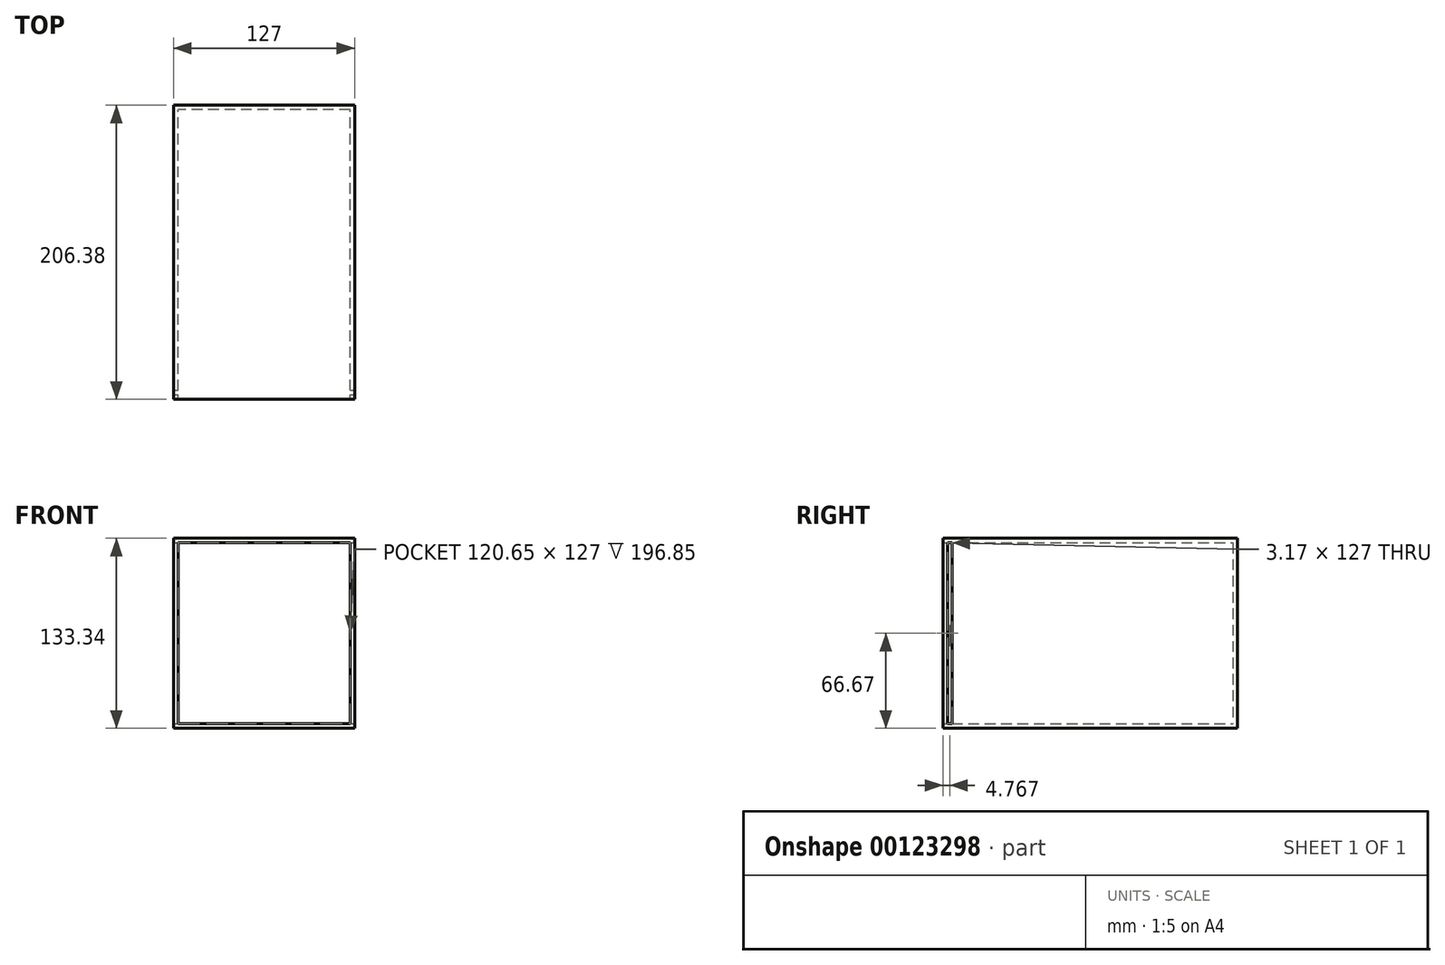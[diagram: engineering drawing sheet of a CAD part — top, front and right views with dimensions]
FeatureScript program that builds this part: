
annotation { "Feature Type Name" : "Feature", "Feature Type Description" : "" }
export const myFeature = defineFeature(function(context is Context, id is Id, definition is map)
    precondition{}
    {
        {
            var Q0;
            Q0=qCreatedBy(makeId("Front.planeOp"),FACE);
            var sketch = newSketch(context, id + "F0", { "sketchPlane" : qUnion([Q0])});
            skLineSegment(sketch, "E0.bottom", {"start": v(63.5, -63.5) * mm, "end": v(-63.5, -63.5) * mm});
            skLineSegment(sketch, "E0.top", {"start": v(63.5, 63.5) * mm, "end": v(-63.5, 63.5) * mm});
            skLineSegment(sketch, "E0.left", {"start": v(63.5, -63.5) * mm, "end": v(63.5, 63.5) * mm});
            skLineSegment(sketch, "E0.right", {"start": v(-63.5, -63.5) * mm, "end": v(-63.5, 63.5) * mm});
            skPoint(sketch, "E0.middle", {"position": v(0, 0) * mm});
            skSolve(sketch);
        }
        {
            var Q0;
            Q0 = qSketchRegion(id + "F0", true);
            extrude(context, id + "F1", {"entities" : qUnion([Q0]), "depth" : 3.17 * mm});
        }
        {
            var Q0;
            Q0=makeQuery(id+"F1.opExtrude","CAP_FACE",FACE,{"disambiguationData":[OSD([sQuery(id+"F0.wireOp",EDGE,"E0.bottom"),sQuery(id+"F0.wireOp",EDGE,"E0.top"),sQuery(id+"F0.wireOp",EDGE,"E0.left"),sQuery(id+"F0.wireOp",EDGE,"E0.right")])],"isStart":false});
            var sketch = newSketch(context, id + "F2", { "sketchPlane" : qUnion([Q0])});
            skLineSegment(sketch, "E1.bottom", {"start": v(-63.5, 63.5) * mm, "end": v(-60.32, 63.5) * mm});
            skLineSegment(sketch, "E1.top", {"start": v(-63.5, -63.5) * mm, "end": v(-60.32, -63.5) * mm});
            skLineSegment(sketch, "E1.left", {"start": v(-63.5, 63.5) * mm, "end": v(-63.5, -63.5) * mm});
            skLineSegment(sketch, "E1.right", {"start": v(-60.32, 63.5) * mm, "end": v(-60.32, -63.5) * mm});
            skLineSegment(sketch, "E2", {"start": v(0, 0) * mm, "end": v(0, 63.5) * mm, "construction": true});
            skLineSegment(sketch, "E3.MirrorCS", {"start": v(60.32, 63.5) * mm, "end": v(60.32, -63.5) * mm});
            skLineSegment(sketch, "E4.MirrorCS", {"start": v(63.5, 63.5) * mm, "end": v(60.32, 63.5) * mm});
            skLineSegment(sketch, "E5.MirrorCS", {"start": v(63.5, 63.5) * mm, "end": v(63.5, -63.5) * mm});
            skLineSegment(sketch, "E6.MirrorCS", {"start": v(63.5, -63.5) * mm, "end": v(60.32, -63.5) * mm});
            skSolve(sketch);
        }
        {
            var Q0;
            Q0 = qSketchRegion(id + "F2", true);
            extrude(context, id + "F3", {"entities" : qUnion([Q0]), "operationType" : NewBodyOperationType.ADD, "depth" : 203.2 * mm});
        }
        {
            var Q0;
            Q0=makeQuery(id+"F3.boolean.opBoolean","MERGE",FACE,{"derivedFrom":[makeQuery(id+"F1.opExtrude","SWEPT_FACE",FACE,{"disambiguationData":[OSD([sQuery(id+"F0.wireOp",EDGE,"E0.top")])]}),makeQuery(id+"F3.opExtrude","SWEPT_FACE",FACE,{"disambiguationData":[OSD([sQuery(id+"F2.wireOp",EDGE,"E1.bottom")])]}),makeQuery(id+"F3.opExtrude","SWEPT_FACE",FACE,{"disambiguationData":[OSD([sQuery(id+"F2.wireOp",EDGE,"E4.MirrorCS")])]})]});
            var sketch = newSketch(context, id + "F4", { "sketchPlane" : qUnion([Q0])});
            skLineSegment(sketch, "E7.bottom", {"start": v(-63.5, 0) * mm, "end": v(63.5, 0) * mm});
            skLineSegment(sketch, "E7.top", {"start": v(-63.5, -206.38) * mm, "end": v(63.5, -206.38) * mm});
            skLineSegment(sketch, "E7.left", {"start": v(-63.5, 0) * mm, "end": v(-63.5, -206.38) * mm});
            skLineSegment(sketch, "E7.right", {"start": v(63.5, 0) * mm, "end": v(63.5, -206.38) * mm});
            skSolve(sketch);
        }
        {
            var Q0;
            Q0 = qSketchRegion(id + "F4", true);
            extrude(context, id + "F5", {"entities" : qUnion([Q0]), "operationType" : NewBodyOperationType.ADD, "depth" : 3.17 * mm});
        }
        {
            var Q0;
            Q0=makeQuery(id+"F3.boolean.opBoolean","MERGE",FACE,{"derivedFrom":[makeQuery(id+"F1.opExtrude","SWEPT_FACE",FACE,{"disambiguationData":[OSD([sQuery(id+"F0.wireOp",EDGE,"E0.bottom")])]}),makeQuery(id+"F3.opExtrude","SWEPT_FACE",FACE,{"disambiguationData":[OSD([sQuery(id+"F2.wireOp",EDGE,"E1.top")])]}),makeQuery(id+"F3.opExtrude","SWEPT_FACE",FACE,{"disambiguationData":[OSD([sQuery(id+"F2.wireOp",EDGE,"E6.MirrorCS")])]})]});
            var sketch = newSketch(context, id + "F6", { "sketchPlane" : qUnion([Q0])});
            skLineSegment(sketch, "E8.bottom", {"start": v(-63.5, 0) * mm, "end": v(63.5, 0) * mm});
            skLineSegment(sketch, "E8.top", {"start": v(-63.5, 206.38) * mm, "end": v(63.5, 206.38) * mm});
            skLineSegment(sketch, "E8.left", {"start": v(-63.5, 0) * mm, "end": v(-63.5, 206.38) * mm});
            skLineSegment(sketch, "E8.right", {"start": v(63.5, 0) * mm, "end": v(63.5, 206.38) * mm});
            skSolve(sketch);
        }
        {
            var Q0;
            Q0 = qSketchRegion(id + "F6", true);
            extrude(context, id + "F7", {"entities" : qUnion([Q0]), "operationType" : NewBodyOperationType.ADD, "depth" : 3.17 * mm});
        }
        {
            var Q0;
            Q0=makeQuery(id+"F7.boolean.opBoolean","MERGE",FACE,{"derivedFrom":[makeQuery(id+"F5.boolean.opBoolean","MERGE",FACE,{"derivedFrom":[makeQuery(id+"F3.boolean.opBoolean","MERGE",FACE,{"derivedFrom":[makeQuery(id+"F1.opExtrude","SWEPT_FACE",FACE,{"disambiguationData":[OSD([sQuery(id+"F0.wireOp",EDGE,"E0.left")])]}),makeQuery(id+"F3.opExtrude","SWEPT_FACE",FACE,{"disambiguationData":[OSD([sQuery(id+"F2.wireOp",EDGE,"E5.MirrorCS")])]})]}),makeQuery(id+"F5.opExtrude","SWEPT_FACE",FACE,{"disambiguationData":[OSD([sQuery(id+"F4.wireOp",EDGE,"E7.right")])]})]}),makeQuery(id+"F7.opExtrude","SWEPT_FACE",FACE,{"disambiguationData":[OSD([sQuery(id+"F6.wireOp",EDGE,"E8.right")])]})]});
            var sketch = newSketch(context, id + "F8", { "sketchPlane" : qUnion([Q0])});
            skLineSegment(sketch, "E9.bottom", {"start": v(-203.2, 63.5) * mm, "end": v(-200.03, 63.5) * mm});
            skLineSegment(sketch, "E9.top", {"start": v(-203.2, -63.5) * mm, "end": v(-200.03, -63.5) * mm});
            skLineSegment(sketch, "E9.left", {"start": v(-203.2, 63.5) * mm, "end": v(-203.2, -63.5) * mm});
            skLineSegment(sketch, "E9.right", {"start": v(-200.03, 63.5) * mm, "end": v(-200.03, -63.5) * mm});
            skSolve(sketch);
        }
        {
            var Q0;
            Q0 = qSketchRegion(id + "F8", true);
            extrude(context, id + "F9", {"entities" : qUnion([Q0]), "operationType" : NewBodyOperationType.REMOVE, "endBound" : BoundingType.THROUGH_ALL, "oppositeDirection" : true, "depth" : 25.4 * mm});
        }
    });
